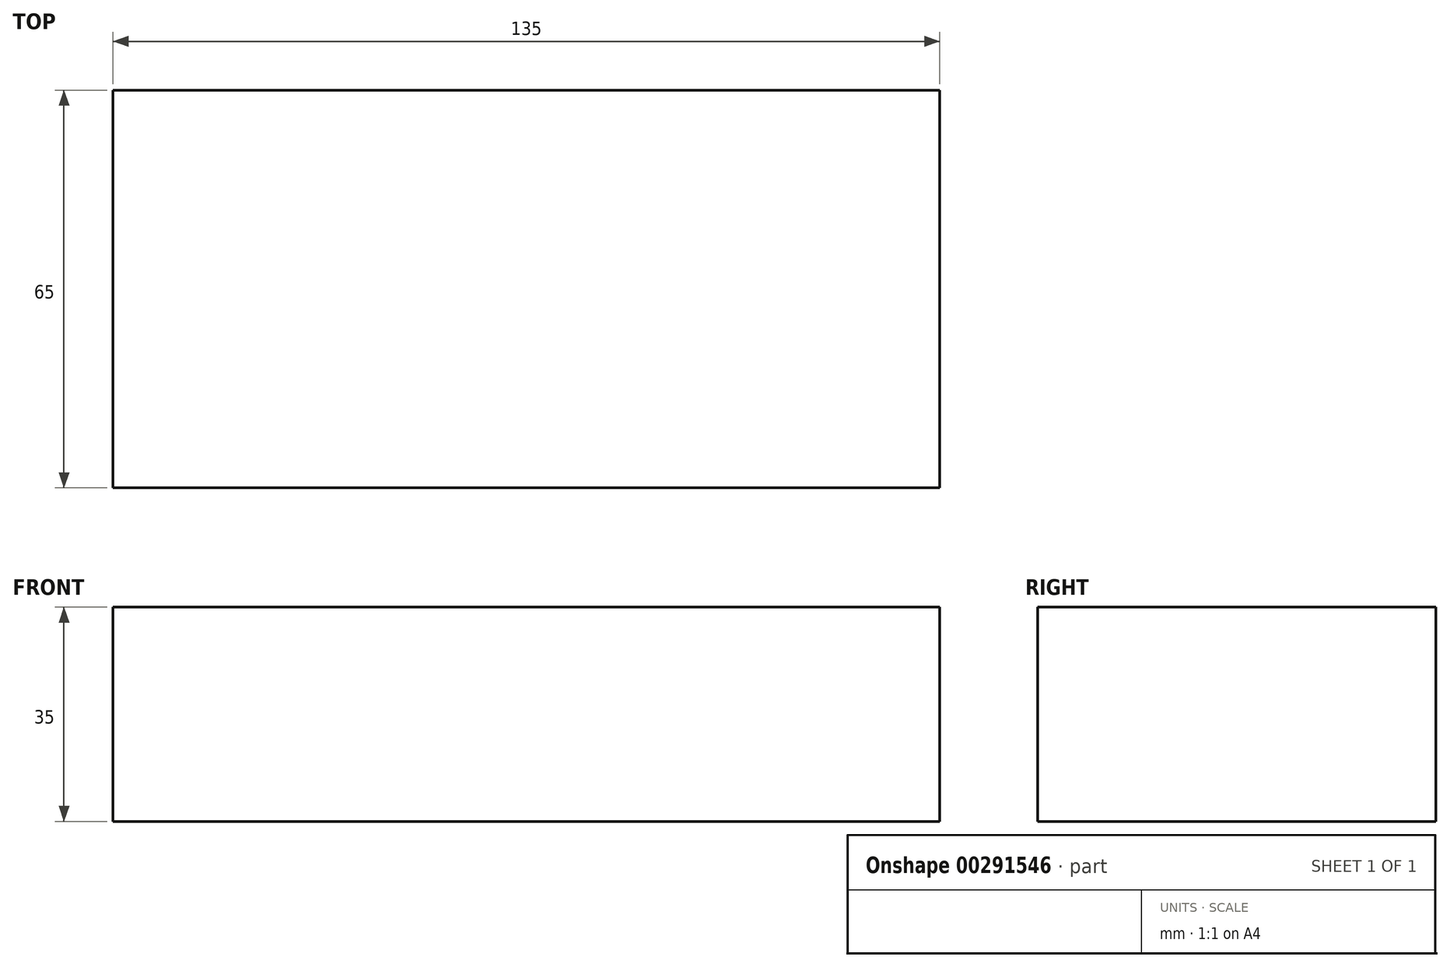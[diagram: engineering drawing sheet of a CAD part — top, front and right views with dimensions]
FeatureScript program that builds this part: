
annotation { "Feature Type Name" : "Feature", "Feature Type Description" : "" }
export const myFeature = defineFeature(function(context is Context, id is Id, definition is map)
    precondition{}
    {
        {
            var Q0;
            Q0=qCreatedBy(makeId("Right.planeOp"),FACE);
            var sketch = newSketch(context, id + "F0", { "sketchPlane" : qUnion([Q0])});
            skLineSegment(sketch, "E0.bottom", {"start": v(-32.5, 17.5) * mm, "end": v(32.5, 17.5) * mm});
            skLineSegment(sketch, "E0.top", {"start": v(-32.5, -17.5) * mm, "end": v(32.5, -17.5) * mm});
            skLineSegment(sketch, "E0.left", {"start": v(-32.5, 17.5) * mm, "end": v(-32.5, -17.5) * mm});
            skLineSegment(sketch, "E0.right", {"start": v(32.5, 17.5) * mm, "end": v(32.5, -17.5) * mm});
            skSolve(sketch);
        }
        {
            var Q0;
            Q0=makeQuery(id+"F0.imprint","IMPRINT",FACE,{"disambiguationData":[TD([[makeQuery(id+"F0.imprint","IMPRINT",EDGE,{"derivedFrom":sQuery(id+"F0.wireOp",EDGE,"E0.bottom")}),-1.0]])]});
            extrude(context, id + "F1", {"entities" : qUnion([Q0]), "endBound" : BoundingType.SYMMETRIC, "depth" : 135 * mm});
        }
    });
